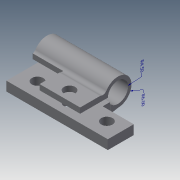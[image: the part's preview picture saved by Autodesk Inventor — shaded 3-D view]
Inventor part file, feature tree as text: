
AUTODESK INVENTOR PART (.ipt)
format: ipt  version: 2019 (Build 230136000, 136)  size: 524,288 bytes
history: native  units: mm
features: extrude x29, sketch x27, other x16, projected_geometry x11, plane x9, direct_edit x8, move_body x4, fillet x3, reference x3, split x2, boolean_combine x1
ambient origin geometry x8: Origin, YZ Plane, XZ Plane, XY Plane, X Axis, Y Axis, Z Axis, Center Point
bodies: Solid1 (feature_tree), Solid2 (feature_tree), Solid3 (feature_tree), Solid4 (feature_tree), Solid5 (feature_tree)
feature tree (113):
  other  "Annotations"
  extrude  "Extrusion1"  Depth=45.0mm
  extrude  "Extrusion4"  Depth=5.0mm
  fillet  "Fillet1"  Radius=11.0mm
  extrude  "Extrusion5"  Depth=23.0mm
  plane  "Work Plane1"
  extrude  "Extrusion6"  Depth=10.0mm
  direct_edit  "Direct Edit1"
  extrude  "Extrusion7"  Depth=12.0mm
  fillet  "Fillet2"  Radius=5.0mm
  plane  "Work Plane5"
  extrude  "Extrusion8"  Depth=5.0mm
  plane  "Work Plane6"
  extrude  "Extrusion9"  Depth=17.8mm
  sketch  "Sketch12"  dims[d34=5.0mm d35=17.8mm]
  extrude  "Extrusion12"  Depth=8.0mm
  extrude  "Extrusion13"  Depth=30.8mm
  extrude  "Extrusion15"  Depth=3.0mm TaperAngle=0.0deg
  plane  "Work Plane7"
  extrude  "Extrusion16"  TaperAngle=0.0deg  [1 undecoded]
  extrude  "Extrusion17"  Depth=18.0mm
  plane  "Work Plane8"
  plane  "Work Plane9"
  split  "Split1"
  split  "Split2"
  boolean_combine  "Combine1"
  direct_edit  "Direct Edit2"
  extrude  "Extrusion18"  Depth=2.0mm
  extrude  "Extrusion20"  Depth=0.5mm TaperAngle=0.0deg
  extrude  "Extrusion21"  Depth=7.25mm TaperAngle=0.0deg
  extrude  "Extrusion22"  Depth=7.25mm TaperAngle=0.0deg
  extrude  "Extrusion23"  Depth=10.0mm TaperAngle=0.0deg
  extrude  "Extrusion24"  Depth=10.0mm
  direct_edit  "Direct Edit3"
  extrude  "Extrusion25"  [1 undecoded]
  sketch  "Sketch24"  dims[d80=10.0mm d81=0.0mm d82=15.0mm]
  plane  "Work Plane10"
  extrude  "Extrusion26"  Depth=3.15mm TaperAngle=0.0deg
  sketch  "Sketch25"  dims[d83=3.0mm d88=-6.0mm]
  plane  "Work Plane11"
  extrude  "Extrusion27"  TaperAngle=0.0deg  [1 undecoded]
  sketch  "Sketch26"  dims[d89=7.5mm d90=3.15mm d91=0.0mm]
  extrude  "Extrusion28"  TaperAngle=0.0deg  [1 undecoded]
  extrude  "Extrusion29"  TaperAngle=0.0deg  [1 undecoded]
  direct_edit  "Direct Edit4"
  sketch  "Sketch28"  dims[d95=0.0mm d96=0.0mm d97=0.0mm d98=-0.3mm]
  plane  "Work Plane12"
  extrude  "Extrusion30"  Depth=10.0mm TaperAngle=0.0deg
  direct_edit  "Direct Edit5"
  extrude  "Extrusion31"  Depth=1.45mm TaperAngle=0.0deg
  extrude  "Extrusion32"  Depth=0.105mm TaperAngle=0.0deg
  direct_edit  "Direct Edit6"
  direct_edit  "Direct Edit7"
  direct_edit  "Direct Edit8"
  extrude  "Extrusion33"  Depth=4.5mm TaperAngle=0.0deg
  extrude  "Extrusion34"  Depth=4.5mm TaperAngle=0.0deg
  fillet  "Fillet6"  Radius=0.105mm
  extrude  "Extrusion35"  TaperAngle=0.0deg  [1 undecoded]
  sketch  "Sketch1"  dims[d0=6.0mm d1=0.0mm d4=45.0mm]
  sketch  "Sketch5"  dims[d5=5.0mm d6=5.0mm d7=11.0mm]
  sketch  "Sketch6"  dims[d8=11.0mm d9=23.0mm]
  sketch  "Sketch7"  dims[d10=10.0mm d20=13.0mm]
  sketch  "Sketch8"  dims[d24=3.0mm d25=0.0mm d26=12.0mm d27=5.0mm]
  sketch  "Sketch10"  dims[d28=3.0mm d29=0.0mm d33=5.0mm]
  projected_geometry  "Projected Loop2"
  sketch  "Sketch13"  dims[d36=8.0mm d37=17.8mm]
  sketch  "Sketch14"  dims[d38=7.1mm d39=30.8mm]
  sketch  "Sketch15"  dims[d40=7.1mm d41=3.0mm d42=0.0mm]
  sketch  "Sketch17"  dims[d46=0.0mm d47=0.0mm d48=-2.5mm d49=0.0mm d50=0.0mm d51=-2.5mm]
  sketch  "Sketch18"  dims[d52=18.0mm d53=11.0mm]
  sketch  "Sketch19"  dims[d54=2.0mm d55=0.0mm d56=2.0mm]
  projected_geometry  "Projected Loop5"
  sketch  "Sketch20"  dims[d57=0.0mm d58=0.5mm d59=0.0mm]
  projected_geometry  "Projected Loop6"
  sketch  "Sketch21"  dims[d60=0.0mm d61=7.25mm d62=0.0mm]
  projected_geometry  "Projected Loop7"
  sketch  "Sketch22"  dims[d68=5.0mm d69=7.25mm d70=0.0mm]
  projected_geometry  "Projected Loop8"
  sketch  "Sketch23"  dims[d72=2.0mm d73=10.0mm d74=0.0mm]
  reference  "Reference1"
  projected_geometry  "Projected Loop9"
  reference  "Reference3"
  reference  "Reference4"
  sketch  "Sketch27"  dims[d92=2.0mm d93=0.0mm d94=0.0mm]
  projected_geometry  "Projected Loop10"
  sketch  "Sketch29"  dims[d99=0.3mm d100=0.0mm]
  projected_geometry  "Projected Loop11"
  sketch  "Sketch30"  dims[d101=10.0mm d102=0.0mm d105=10.0mm d106=0.0mm]
  projected_geometry  "Projected Loop12"
  sketch  "Sketch32"  dims[d110=1.45mm d111=0.0mm d112=1.45mm d113=0.0mm]
  sketch  "Sketch33"  dims[d114=1.65mm d115=0.0mm d116=0.105mm d117=0.0mm]
  projected_geometry  "Projected Loop13"
  sketch  "Sketch34"  dims[d118=-0.105mm d119=0.105mm d120=0.0mm d121=0.105mm d122=0.0mm d123=0.105mm d124=0.0mm d125=0.0mm d126=0.0mm d127=0.105mm d128=0.0mm d129=-2.0mm d130=10.0mm d131=0.0mm d132=0.0mm d133=0.0mm d134=1.76mm d135=1.0mm d136=0.0mm d137=1.0mm d138=0.0mm d140=-0.5mm d143=1.0mm d144=-1.0mm d145=3.4mm d146=1.0mm d147=-1.0mm d148=10.0mm d149=0.0mm d150=10.0mm d151=0.0mm d152=4.0mm d153=10.0mm d154=0.0mm d84=49.911908mm d85=6.0mm d86=52.109261mm d87=4.5mm]
  projected_geometry  "Projected Loop14"
  other  "Composite1"
  move_body  "Move1"
  move_body  "Move2"
  move_body  "Move3"
  other  "Size1"
  other  "Srf1"
  parser-record x1  (decoder bookkeeping rows leaked as tree rows — omitted from the tree; the rows remain in map.json)
  other  "Cerniera versione 3.iam"
  other  "Cerniera 5.5:1"
  other  "Size2"
  move_body  "Move4"
  other  "Size3"
  other  "Size4"
  other  "Size5"
  other  "Size6"
  other  "Size7"
  other  "Size8"
  other  "Radial Dimension 1"
  other  "Radial Dimension 2"
note: 6 required parameter values undecoded (feature->parameter linkage not recoverable at this tier; creation-order binding heuristic only, values carry confidence <= 0.55)
note: 1 file-system path scrubbed to <path> (originals preserved in map.json)
